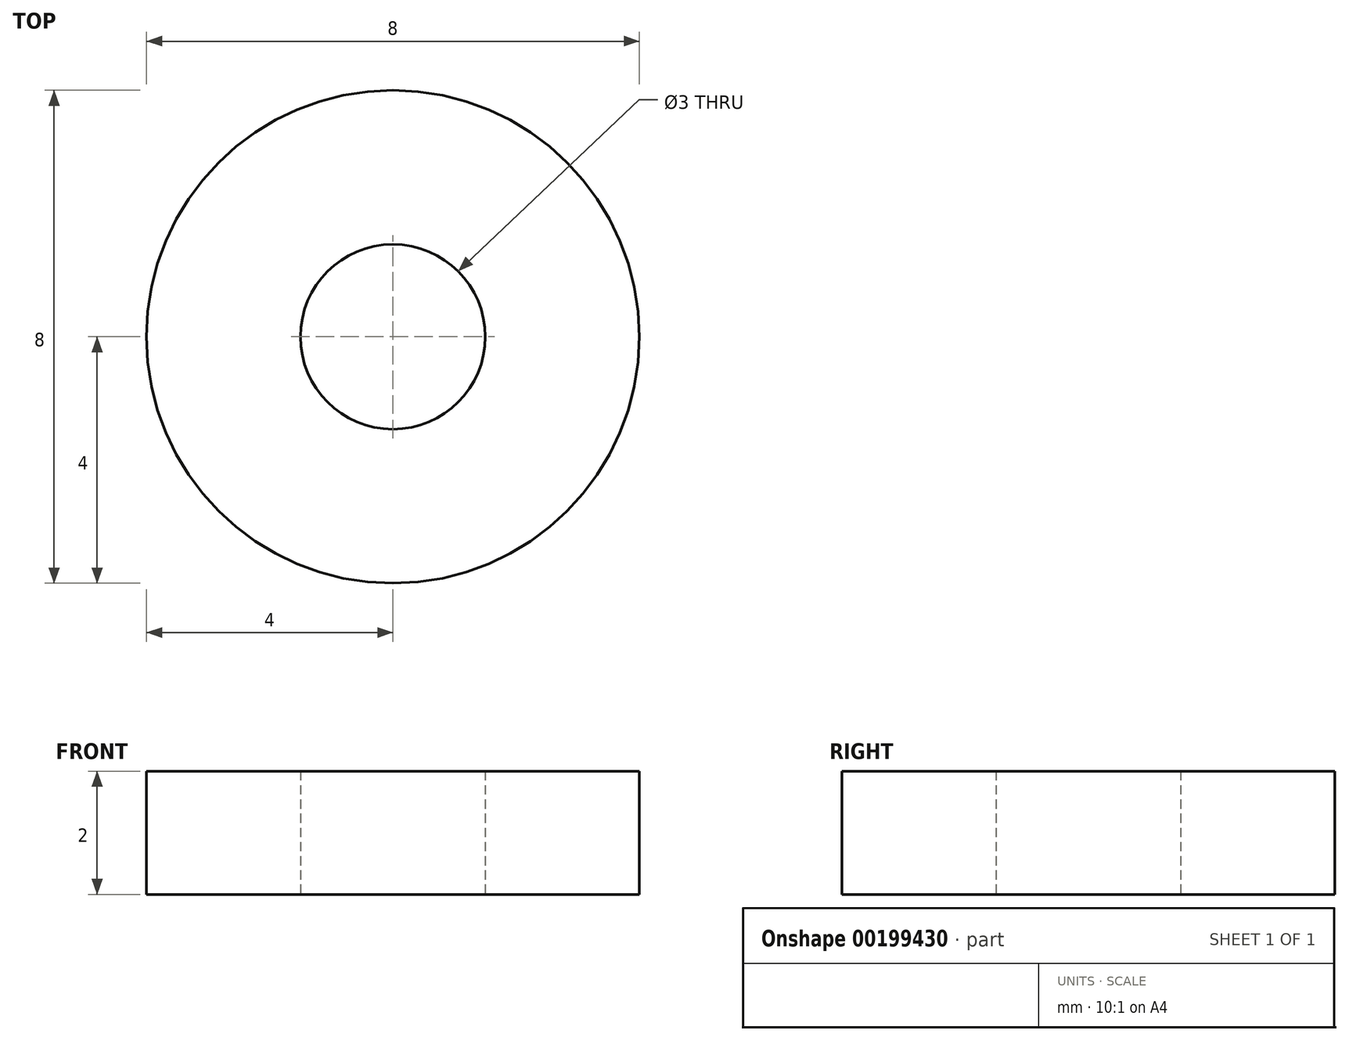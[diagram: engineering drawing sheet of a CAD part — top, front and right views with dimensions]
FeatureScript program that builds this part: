
annotation { "Feature Type Name" : "Feature", "Feature Type Description" : "" }
export const myFeature = defineFeature(function(context is Context, id is Id, definition is map)
    precondition{}
    {
        {
            var Q0;
            Q0=qCreatedBy(makeId("Top.planeOp"),FACE);
            var sketch = newSketch(context, id + "F0", { "sketchPlane" : qUnion([Q0])});
            skCircle(sketch, "E0", {"center": v(0, 0) * mm, "radius": 4 * mm});
            skCircle(sketch, "E1", {"center": v(0, 0) * mm, "radius": 1.5 * mm});
            skSolve(sketch);
        }
        {
            var Q0;
            Q0 = qSketchRegion(id + "F0", true);
            extrude(context, id + "F1", {"entities" : qUnion([Q0]), "depth" : 2 * mm});
        }
    });
